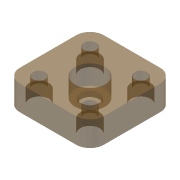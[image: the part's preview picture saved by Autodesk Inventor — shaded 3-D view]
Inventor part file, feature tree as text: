
AUTODESK INVENTOR PART (.ipt)
format: ipt  version: 2018 (Build 220112000, 112)  size: 145,920 bytes
history: native  units: in
note: dims shown in document units (in); Inventor stores cm internally (conversion verified against a paired STEP export)
features: hole x5, fillet x4, extrude x1, sketch x1
ambient origin geometry x8: Origin, YZ Plane, XZ Plane, XY Plane, X Axis, Y Axis, Z Axis, Center Point
bodies: Solid1 (feature_tree)
feature tree (11):
  extrude  "Extrusion1"  Depth=1.2008in
  hole  "Hole5"  [1 undecoded]
  fillet  "Fillet1"  Radius=0.1969in
  fillet  "Fillet2"  Radius=0.1969in
  fillet  "Fillet3"  Radius=0.1969in
  fillet  "Fillet4"  Radius=0.1969in
  hole  "Hole10"  [1 undecoded]
  hole  "Hole11"  [1 undecoded]
  hole  "Hole12"  [1 undecoded]
  hole  "Hole13"  [1 undecoded]
  sketch  "Sketch1"  dims[d0=1.2008in d1=1.2008in d2=0.3543in d3=0.0in d40=0.6004in d41=0.6004in d42=0.2559in d43=0.2362in d44=0.4331in d45=0.2756in d46=90.0deg d47=0.315in d48=0.8108in d49=0.1969in d50=0.1969in d51=0.1969in d52=0.1969in d89=0.2362in d90=0.2362in d91=0.1772in d92=0.2362in d93=0.2756in d94=0.1969in d95=90.0deg d96=0.315in d97=0.8108in d98=0.2362in d99=0.2362in d100=0.1772in d101=0.2362in d102=0.2756in d103=0.1969in d104=90.0deg d105=0.315in d106=0.8108in d107=0.2362in d108=0.2362in d109=0.1772in d110=0.2362in d111=0.2756in d112=0.1969in d113=90.0deg d114=0.315in d115=0.8108in d116=0.2362in d117=0.2362in d118=0.1772in d119=0.2362in d120=0.2756in d121=0.1969in d122=90.0deg d123=0.315in d124=0.8108in]
note: 5 required parameter values undecoded (feature->parameter linkage not recoverable at this tier; creation-order binding heuristic only, values carry confidence <= 0.55)
